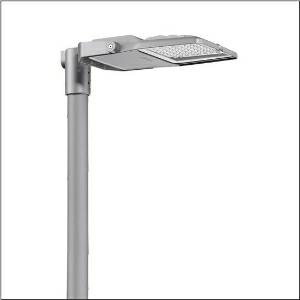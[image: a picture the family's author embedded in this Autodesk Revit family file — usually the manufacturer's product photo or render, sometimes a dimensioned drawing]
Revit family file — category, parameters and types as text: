
# Revit family: floodlight_fl_21_iq_mini___pl33t_5xa7772c2f3a_076b
name_source: partatom
category: Lighting Fixtures
units: mm (PartAtom-declared; Revit-internal decimal feet)

## family parameters
Cut with Voids When Loaded = No
Host = Face
Light Source = No
Part Type = Normal
Room Calculation Point = No
Round Connector Dimension = Use Diameter
Shared = No

## types (1)
- --- (1 x LED, 12060 lm, 87.2 W, 3000K)
    Apparent Load = 87 VA
    CIE Flux Codes = 26 75 99 100 100
    Color Rendering = 70
    Color Temperature = 3000K
    Default Elevation = 1800 mm
    Description = Floodlight FL 21 iQ mini, floodlight, primary light control with lens, of PMMA, primary optical cover: protective disc, of toughened safety glass, transparent, light distribution: PL33T, light emission: direct distribution, installation type: surface-mounted, lamps: LED, High Power LED, rated values: 12.060lm | 87,2W | 138,3lm/W (begin service life); end service life: 12.060lm | 92,1W; at 50% lumin. flux: 6.030lm | 40,1W | 150,4lm/W, colour temperature: 3000K, colour rendering: CRI > 70, light colour: 730, light setting 1 begin service life: 100% | 12.060lm | 87,2W | 138,3lm/W | 3.000K, light setting 1 end service life: 92,1W, further light settings possible, control: pre-setting: linear dimming characteristic, Auto-Match, Temp-Guard, Night-Set, Smart-Wire, Desk-Remote (wireless, voltage-free reading and setting of iQ features in the workshop via application-optimized NFC function/RFID function), optimised constant luminous flux control (CLO 2.0), Light-Fading, Lumen-Switch, with terminal, 6-pole, mains connection: 220..240V, AC, 50/60Hz, luminaire housing, of diecast aluminium, powder-coated, SITECO metallic grey (DB 702S), corrosivity category C5 mid according to DIN EN ISO 12944suitable for swimming poolschlorine-resistant, sealing non-destructively replaceable, please order mast flange separately, mast bracket, of steel, galvanised, powder-coated, protection rating (complete): IP66, insulation class (complete): insulation class II (safety insulation), certification: CE, ENEC, VDE, protection symbol: D, impact resistance: IK08, permissible operating ambient temperature: -40..+40°C, permissible operating ambient temperature for outdoor applications: -40..+50°C, standard: DIN EN 12944, LABS conformity tested according to VDMA 24364:2018-05, packaging unit: 1 piece

Light Distribution: PL33T
    Height = 70 mm
    Lamp = 1 x LED
    Lamp Light Flux = 12060 lm
    Lamp Power = 87.2 W
    Lamp count = 1
    Length = 485 mm
    Luminous efficacy = 138 lm/W
    Manufacturer = Siteco
    ModVariant = No
    Model = 5XA7772C2F3A
    Number of Poles = 1
    OnlyDefault = Yes
    Power Factor = 1
    Product Name = Floodlight FL 21 iQ mini | PL33T
    Product group = floodlight | pylon annexe
    ProductGroupID = 6201
    Protection Class = Protection class II
    Protection Degree = IP 66
    RLX_Detail_Level = 1
    RLX_Emergency_Light_Flux = 0 lm
    RLX_Emergency_Type = 0
    RLX_Emergency_Type_DB = No
    RlxData = <blob elided: 101501 chars, md5=abc17dbb>
    Socket = socket
    Standby Power = 0 W
    System Light Flux = 12060 lm
    System Power = 87 W
    Type Comments = factory setting: luminous flux: 100 % | dim-lin: 254 | 456 mA
    Type Image = l_1007125.jpg
    URL = http://relux.com
    VarID = @adj_148987
    Voltage = 0 V
    Weight = 0.00 kg
    Width = 337 mm

## geometry (parser evidence)
native form markers: Blend x4, Sweep x12
no freeform markers — native parametric forms only
